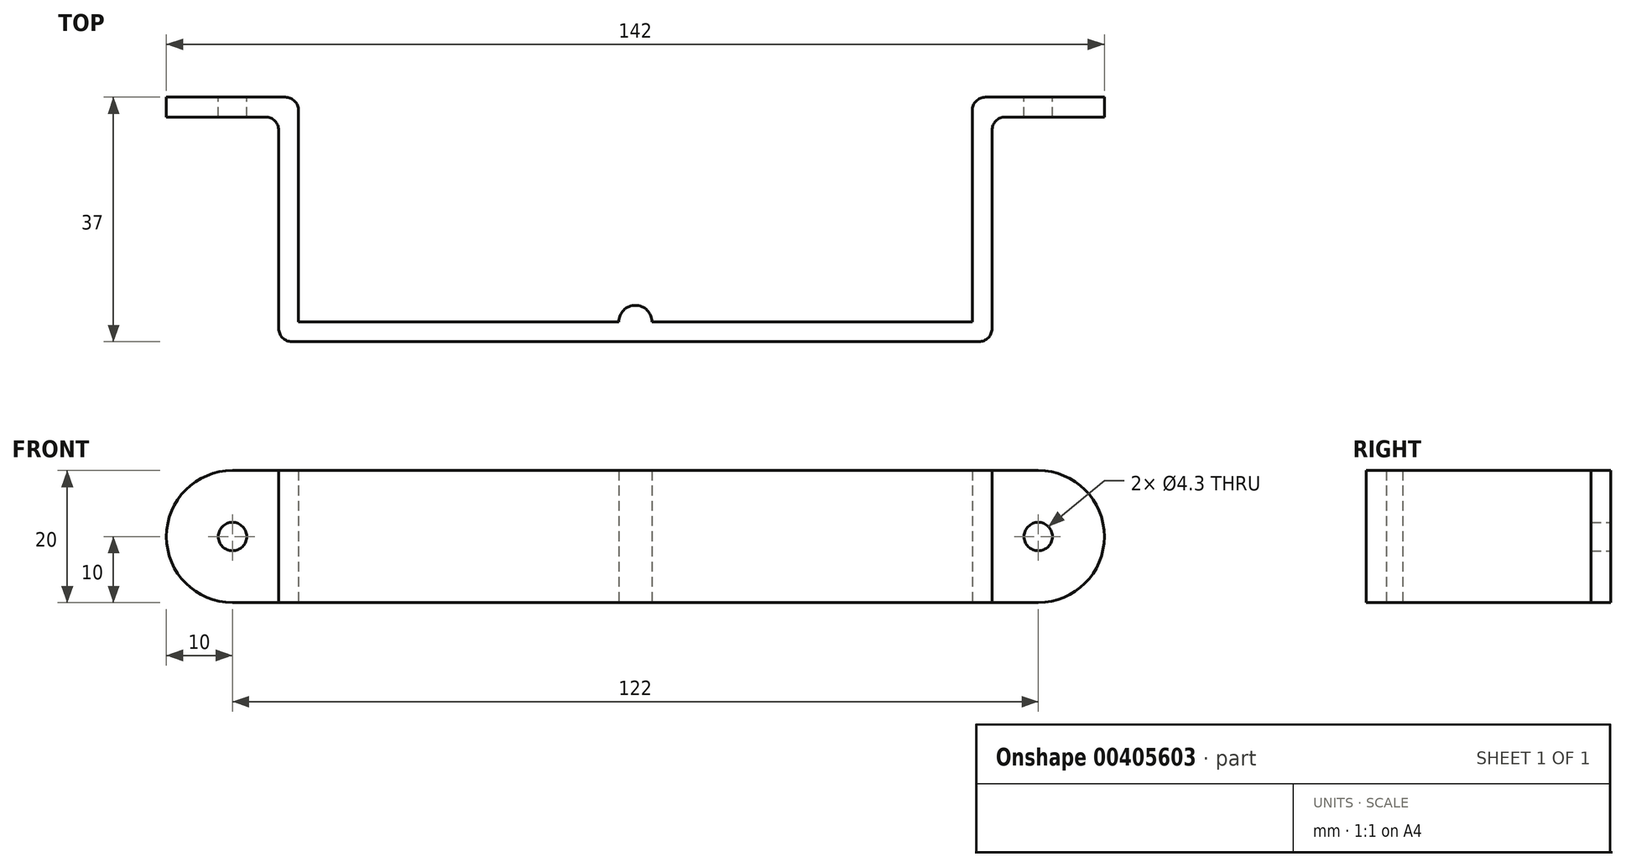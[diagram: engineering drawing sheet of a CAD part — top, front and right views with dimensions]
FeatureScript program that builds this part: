
annotation { "Feature Type Name" : "Feature", "Feature Type Description" : "" }
export const myFeature = defineFeature(function(context is Context, id is Id, definition is map)
    precondition{}
    {
        {
            assignVariable(context, id + "F0", {"name" : "width", "anyValue" : 20});
        }
        {
            assignVariable(context, id + "F1", {"name" : "thickness", "anyValue" : 3});
        }
        {
            var Q0;
            Q0=qCreatedBy(makeId("Top.planeOp"),FACE);
            var sketch = newSketch(context, id + "F2", { "sketchPlane" : qUnion([Q0])});
            skLineSegment(sketch, "E0", {"start": v(51, 0) * mm, "end": v(51, 34) * mm});
            skLineSegment(sketch, "E1", {"start": v(51, 34) * mm, "end": v(71, 34) * mm});
            skArc(sketch, "E2", {"start": v(0, 2.5) * mm, "mid": v(1.77, 1.77) * mm, "end": v(2.5, 0) * mm});
            skLineSegment(sketch, "E3", {"start": v(2.5, 0) * mm, "end": v(51, 0) * mm});
            skLineSegment(sketch, "E4", {"start": v(71, 34) * mm, "end": v(71, 31) * mm});
            skLineSegment(sketch, "E5", {"start": v(71, 31) * mm, "end": v(54, 31) * mm});
            skLineSegment(sketch, "E6", {"start": v(54, 31) * mm, "end": v(54, -3) * mm});
            skLineSegment(sketch, "E7", {"start": v(54, -3) * mm, "end": v(0, -3) * mm});
            skLineSegment(sketch, "E8", {"start": v(0, -3) * mm, "end": v(0, 2.5) * mm});
            skSolve(sketch);
        }
        {
            var Q0;
            Q0=makeQuery(id+"F2.imprint","IMPRINT",FACE,{"disambiguationData":[TD([[makeQuery(id+"F2.imprint","IMPRINT",EDGE,{"derivedFrom":sQuery(id+"F2.wireOp",EDGE,"E0")}),-1.0]])]});
            extrude(context, id + "F3", {"entities" : qUnion([Q0]), "depth" : (getVariable(context, 'width')) * mm});
        }
        {
            var Q0;
            Q0=makeQuery(id+"F3.opExtrude","CAP_EDGE",EDGE,{"disambiguationData":[OSD([sQuery(id+"F2.wireOp",EDGE,"E4")])],"isStart":true});
            var Q1;
            Q1=makeQuery(id+"F3.opExtrude","CAP_EDGE",EDGE,{"disambiguationData":[OSD([sQuery(id+"F2.wireOp",EDGE,"E4")])],"isStart":false});
            fillet(context, id + "F4", {"entities" : qUnion([Q0, Q1]), "radius" : (getVariable(context, 'width') / 2) * mm, "tangentPropagation" : true, "allowEdgeOverflow" : false});
        }
        {
            var Q0;
            Q0=makeQuery(id+"F3.opExtrude","SWEPT_FACE",FACE,{"disambiguationData":[OSD([sQuery(id+"F2.wireOp",EDGE,"E1")])]});
            var sketch = newSketch(context, id + "F5", { "sketchPlane" : qUnion([Q0])});
            skCircle(sketch, "E9", {"center": v(-61, 10) * mm, "radius": 2.15 * mm});
            skSolve(sketch);
        }
        {
            var Q0;
            Q0=makeQuery(id+"F5.imprint","IMPRINT",FACE,{"disambiguationData":[TD([[makeQuery(id+"F5.imprint","IMPRINT",EDGE,{"derivedFrom":sQuery(id+"F5.wireOp",EDGE,"E9")}),1.0]])]});
            extrude(context, id + "F6", {"entities" : qUnion([Q0]), "operationType" : NewBodyOperationType.REMOVE, "oppositeDirection" : true, "depth" : (getVariable(context, 'thickness')) * mm});
        }
        {
            var Q0;
            Q0=makeQuery(id+"F3.opExtrude","SWEPT_BODY",BODY,{"disambiguationData":[OSD([sQuery(id+"F2.wireOp",EDGE,"E0"),sQuery(id+"F2.wireOp",EDGE,"E1"),sQuery(id+"F2.wireOp",EDGE,"E2"),sQuery(id+"F2.wireOp",EDGE,"E3"),sQuery(id+"F2.wireOp",EDGE,"E4"),sQuery(id+"F2.wireOp",EDGE,"E5"),sQuery(id+"F2.wireOp",EDGE,"E6"),sQuery(id+"F2.wireOp",EDGE,"E7"),sQuery(id+"F2.wireOp",EDGE,"E8")])]});
            var Q1;
            Q1=makeQuery(id+"F3.opExtrude","SWEPT_FACE",FACE,{"disambiguationData":[OSD([sQuery(id+"F2.wireOp",EDGE,"E8")])]});
            mirror(context, id + "F7", {"operationType" : NewBodyOperationType.ADD, "entities" : qUnion([Q0]), "mirrorPlane" : qUnion([Q1])});
        }
        {
            var Q0;
            Q0=makeQuery(id+"F3.opExtrude","SWEPT_EDGE",EDGE,{"disambiguationData":[OSD([sQuery(id+"F2.wireOp",EDGE,"E6"),sQuery(id+"F2.wireOp",EDGE,"E7")])]});
            var Q1;
            Q1=makeQuery(id+"F7.opPattern","COPY",EDGE,{"derivedFrom":makeQuery(id+"F3.opExtrude","SWEPT_EDGE",EDGE,{"disambiguationData":[OSD([sQuery(id+"F2.wireOp",EDGE,"E6"),sQuery(id+"F2.wireOp",EDGE,"E7")])]}),"instanceName":"1"});
            var Q2;
            Q2=makeQuery(id+"F3.opExtrude","SWEPT_EDGE",EDGE,{"disambiguationData":[OSD([sQuery(id+"F2.wireOp",EDGE,"E5"),sQuery(id+"F2.wireOp",EDGE,"E6")])]});
            var Q3;
            Q3=makeQuery(id+"F7.opPattern","COPY",EDGE,{"derivedFrom":makeQuery(id+"F3.opExtrude","SWEPT_EDGE",EDGE,{"disambiguationData":[OSD([sQuery(id+"F2.wireOp",EDGE,"E5"),sQuery(id+"F2.wireOp",EDGE,"E6")])]}),"instanceName":"1"});
            var Q4;
            Q4=makeQuery(id+"F3.opExtrude","SWEPT_EDGE",EDGE,{"disambiguationData":[OSD([sQuery(id+"F2.wireOp",EDGE,"E0"),sQuery(id+"F2.wireOp",EDGE,"E1")])]});
            var Q5;
            Q5=makeQuery(id+"F7.opPattern","COPY",EDGE,{"derivedFrom":makeQuery(id+"F3.opExtrude","SWEPT_EDGE",EDGE,{"disambiguationData":[OSD([sQuery(id+"F2.wireOp",EDGE,"E0"),sQuery(id+"F2.wireOp",EDGE,"E1")])]}),"instanceName":"1"});
            fillet(context, id + "F8", {"entities" : qUnion([Q0, Q1, Q2, Q3, Q4, Q5]), "radius" : 2 * mm, "tangentPropagation" : true, "allowEdgeOverflow" : false});
        }
    });
